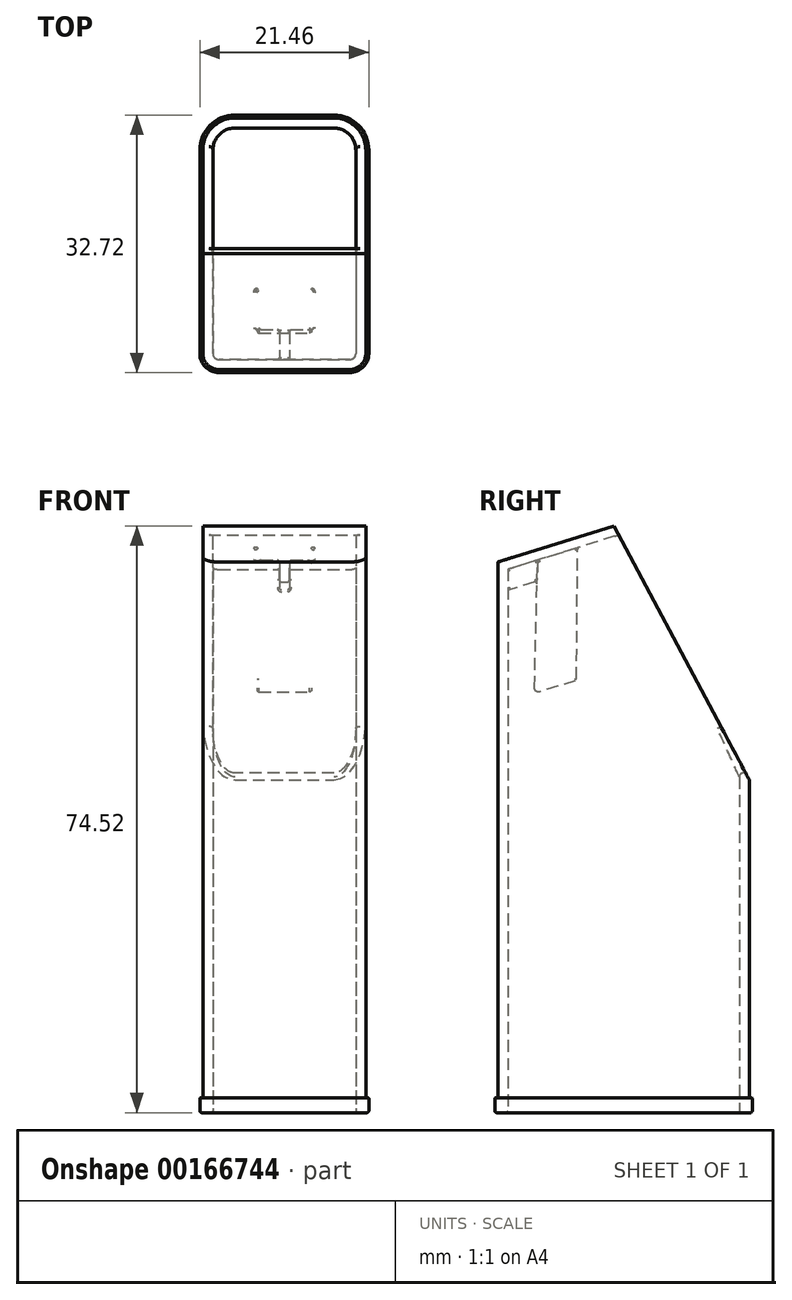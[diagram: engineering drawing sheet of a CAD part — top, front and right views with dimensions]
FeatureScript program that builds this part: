
annotation { "Feature Type Name" : "Feature", "Feature Type Description" : "" }
export const myFeature = defineFeature(function(context is Context, id is Id, definition is map)
    precondition{}
    {
        {
            var Q0;
            Q0=qCreatedBy(makeId("Top.planeOp"),FACE);
            var sketch = newSketch(context, id + "F0", { "sketchPlane" : qUnion([Q0])});
            skLineSegment(sketch, "E0.bottom", {"start": v(10.35, 15.98) * mm, "end": v(-10.35, 15.98) * mm});
            skLineSegment(sketch, "E0.top", {"start": v(10.35, -15.98) * mm, "end": v(-10.35, -15.98) * mm});
            skLineSegment(sketch, "E0.left", {"start": v(10.35, 15.98) * mm, "end": v(10.35, -15.98) * mm});
            skLineSegment(sketch, "E0.right", {"start": v(-10.35, 15.98) * mm, "end": v(-10.35, -15.98) * mm});
            skPoint(sketch, "E0.middle", {"position": v(0, 0) * mm});
            skLineSegment(sketch, "E1.0", {"start": v(10.9, 16.54) * mm, "end": v(-10.9, 16.54) * mm});
            skLineSegment(sketch, "E1.1", {"start": v(10.9, 16.54) * mm, "end": v(10.9, -16.54) * mm});
            skLineSegment(sketch, "E1.2", {"start": v(10.9, -16.54) * mm, "end": v(-10.9, -16.54) * mm});
            skLineSegment(sketch, "E1.3", {"start": v(-10.9, 16.54) * mm, "end": v(-10.9, -16.54) * mm});
            skSolve(sketch);
        }
        {
            var Q0;
            Q0=makeQuery(id+"F0.imprint","IMPRINT",FACE,{"disambiguationData":[TD([[makeQuery(id+"F0.imprint","IMPRINT",EDGE,{"derivedFrom":sQuery(id+"F0.wireOp",EDGE,"E0.bottom")}),1.0]])]});
            extrude(context, id + "F1", {"entities" : qUnion([Q0]), "depth" : 74.52 * mm});
        }
        {
            var Q0;
            Q0=makeQuery(id+"F1.opExtrude","SWEPT_FACE",FACE,{"disambiguationData":[OSD([sQuery(id+"F0.wireOp",EDGE,"E0.left")])]});
            var sketch = newSketch(context, id + "F2", { "sketchPlane" : qUnion([Q0])});
            skLineSegment(sketch, "E2", {"start": v(-1.24, 74.52) * mm, "end": v(-15.98, 69.95) * mm});
            skLineSegment(sketch, "E3", {"start": v(-1.24, 74.52) * mm, "end": v(15.98, 42.3) * mm});
            skSolve(sketch);
        }
        {
            var Q0;
            {var subQ0=sQuery(id+"F2.wireOp",EDGE,"E2");Q0=makeQuery(id+"F2.imprint","IMPRINT",FACE,{"disambiguationData":[TD([[makeQuery(id+"F2.imprint","IMPRINT",EDGE,{"derivedFrom":subQ0}),-1.0]])]});}
            var Q1;
            {var subQ0=sQuery(id+"F2.wireOp",EDGE,"E3");Q1=makeQuery(id+"F2.imprint","IMPRINT",FACE,{"disambiguationData":[TD([[makeQuery(id+"F2.imprint","IMPRINT",EDGE,{"derivedFrom":subQ0}),1.0]])]});}
            extrude(context, id + "F3", {"entities" : qUnion([Q0, Q1]), "operationType" : NewBodyOperationType.REMOVE, "endBound" : BoundingType.UP_TO_NEXT, "oppositeDirection" : true, "depth" : 25.4 * mm});
        }
        {
            var Q0;
            Q0=makeQuery(id+"F1.opExtrude","SWEPT_EDGE",EDGE,{"disambiguationData":[OSD([sQuery(id+"F0.wireOp",EDGE,"E0.top"),sQuery(id+"F0.wireOp",EDGE,"E0.right")])]});
            var Q1;
            Q1=makeQuery(id+"F1.opExtrude","SWEPT_EDGE",EDGE,{"disambiguationData":[OSD([sQuery(id+"F0.wireOp",EDGE,"E0.top"),sQuery(id+"F0.wireOp",EDGE,"E0.left")])]});
            var Q2;
            Q2=makeQuery(id+"F3.boolean.opBoolean","COPY",EDGE,{"derivedFrom":makeQuery(id+"F3.opExtrude","SWEPT_EDGE",EDGE,{"disambiguationData":[OSD([sQuery(id+"F0.wireOp",EDGE,"E0.top"),sQuery(id+"F0.wireOp",EDGE,"E0.left"),sQuery(id+"F2.wireOp",EDGE,"E2")])]})});
            var Q3;
            Q3=makeQuery(id+"F3.boolean.opBoolean","COPY",EDGE,{"derivedFrom":makeQuery(id+"F3.opExtrude","CAP_EDGE",EDGE,{"disambiguationData":[OSD([sQuery(id+"F2.wireOp",EDGE,"E2")])],"isStart":false})});
            var Q4;
            Q4=makeQuery(id+"F3.boolean.opBoolean","COPY",EDGE,{"derivedFrom":makeQuery(id+"F3.opExtrude","CAP_EDGE",EDGE,{"disambiguationData":[OSD([sQuery(id+"F2.wireOp",EDGE,"E2")])],"isStart":true})});
            fillet(context, id + "F4", {"entities" : qUnion([Q0, Q1, Q2, Q3, Q4]), "radius" : 2.03 * mm, "tangentPropagation" : true, "allowEdgeOverflow" : false});
        }
        {
            var Q0;
            Q0=makeQuery(id+"F1.opExtrude","SWEPT_EDGE",EDGE,{"disambiguationData":[OSD([sQuery(id+"F0.wireOp",EDGE,"E0.bottom"),sQuery(id+"F0.wireOp",EDGE,"E0.left")])]});
            var Q1;
            Q1=makeQuery(id+"F1.opExtrude","SWEPT_EDGE",EDGE,{"disambiguationData":[OSD([sQuery(id+"F0.wireOp",EDGE,"E0.bottom"),sQuery(id+"F0.wireOp",EDGE,"E0.right")])]});
            fillet(context, id + "F5", {"entities" : qUnion([Q0, Q1]), "radius" : 4.06 * mm, "tangentPropagation" : true, "allowEdgeOverflow" : false});
        }
        {
            var Q0;
            Q0=makeQuery(id+"F3.boolean.opBoolean","COPY",FACE,{"derivedFrom":makeQuery(id+"F3.opExtrude","SWEPT_FACE",FACE,{"disambiguationData":[OSD([sQuery(id+"F2.wireOp",EDGE,"E3")])]})});
            var Q1;
            Q1=makeQuery(id+"F1.opExtrude","CAP_FACE",FACE,{"disambiguationData":[OSD([sQuery(id+"F0.wireOp",EDGE,"E0.bottom"),sQuery(id+"F0.wireOp",EDGE,"E0.top"),sQuery(id+"F0.wireOp",EDGE,"E0.left"),sQuery(id+"F0.wireOp",EDGE,"E0.right")])],"isStart":true});
            shell(context, id + "F6", {"entities" : qUnion([Q0, Q1]), "thickness" : 1.27 * mm});
        }
        {
            var Q0;
            Q0=makeQuery(id+"F3.boolean.opBoolean","COPY",EDGE,{"derivedFrom":makeQuery(id+"F3.opExtrude","CAP_EDGE",EDGE,{"disambiguationData":[OSD([sQuery(id+"F2.wireOp",EDGE,"E3")])],"isStart":true})});
            var Q1;
            Q1=makeQuery(id+"F6.opShell","OFFSET_EDGE",EDGE,{"disambiguationData":[OSD([sQuery(id+"F2.wireOp",EDGE,"E3")])]});
            fillet(context, id + "F7", {"entities" : qUnion([Q0, Q1]), "radius" : 0.5 * mm, "tangentPropagation" : true, "allowEdgeOverflow" : false});
        }
        {
            var Q0;
            Q0=makeQuery(id+"F1.opExtrude","CAP_FACE",FACE,{"disambiguationData":[OSD([sQuery(id+"F0.wireOp",EDGE,"E0.bottom"),sQuery(id+"F0.wireOp",EDGE,"E0.top"),sQuery(id+"F0.wireOp",EDGE,"E0.left"),sQuery(id+"F0.wireOp",EDGE,"E0.right")])],"isStart":true});
            var sketch = newSketch(context, id + "F8", { "sketchPlane" : qUnion([Q0])});
            skLineSegment(sketch, "E4.0.0", {"start": v(-6.29, -15.98) * mm, "end": v(6.29, -15.98) * mm});
            skArc(sketch, "E4.0.1", {"start": v(6.29, -15.98) * mm, "mid": v(9.16, -14.79) * mm, "end": v(10.35, -11.91) * mm});
            skLineSegment(sketch, "E4.0.2", {"start": v(10.35, -11.91) * mm, "end": v(10.35, 13.94) * mm});
            skArc(sketch, "E4.0.3", {"start": v(10.35, 13.94) * mm, "mid": v(9.76, 15.38) * mm, "end": v(8.32, 15.98) * mm});
            skLineSegment(sketch, "E4.0.4", {"start": v(8.32, 15.98) * mm, "end": v(-8.32, 15.98) * mm});
            skArc(sketch, "E4.0.5", {"start": v(-8.32, 15.98) * mm, "mid": v(-9.76, 15.38) * mm, "end": v(-10.35, 13.94) * mm});
            skLineSegment(sketch, "E4.0.6", {"start": v(-10.35, 13.94) * mm, "end": v(-10.35, -11.91) * mm});
            skArc(sketch, "E4.0.7", {"start": v(-10.35, -11.91) * mm, "mid": v(-9.16, -14.79) * mm, "end": v(-6.29, -15.98) * mm});
            skLineSegment(sketch, "E5.0", {"start": v(8.32, 16.36) * mm, "end": v(-8.32, 16.36) * mm});
            skArc(sketch, "E5.1", {"start": v(10.73, 13.94) * mm, "mid": v(10.02, 15.65) * mm, "end": v(8.32, 16.36) * mm});
            skArc(sketch, "E5.2", {"start": v(-8.32, 16.36) * mm, "mid": v(-10.02, 15.65) * mm, "end": v(-10.73, 13.94) * mm});
            skLineSegment(sketch, "E5.3", {"start": v(10.73, -11.91) * mm, "end": v(10.73, 13.94) * mm});
            skLineSegment(sketch, "E5.4", {"start": v(-10.73, 13.94) * mm, "end": v(-10.73, -11.91) * mm});
            skArc(sketch, "E5.5", {"start": v(-10.73, -11.91) * mm, "mid": v(-9.43, -15.06) * mm, "end": v(-6.29, -16.36) * mm});
            skLineSegment(sketch, "E5.6", {"start": v(-6.29, -16.36) * mm, "end": v(6.29, -16.36) * mm});
            skArc(sketch, "E5.7", {"start": v(6.29, -16.36) * mm, "mid": v(9.43, -15.06) * mm, "end": v(10.73, -11.91) * mm});
            skSolve(sketch);
        }
        {
            var Q0;
            Q0=makeQuery(id+"F8.imprint","IMPRINT",FACE,{"disambiguationData":[TD([[makeQuery(id+"F8.imprint","IMPRINT",EDGE,{"derivedFrom":sQuery(id+"F8.wireOp",EDGE,"E4.0.0")}),1.0]])]});
            extrude(context, id + "F9", {"entities" : qUnion([Q0]), "operationType" : NewBodyOperationType.ADD, "oppositeDirection" : true, "depth" : 1.9 * mm});
        }
        {
            var Q0;
            Q0=makeQuery(id+"F9.boolean.opBoolean","MERGE",FACE,{"derivedFrom":[makeQuery(id+"F1.opExtrude","CAP_FACE",FACE,{"disambiguationData":[OSD([sQuery(id+"F0.wireOp",EDGE,"E0.bottom"),sQuery(id+"F0.wireOp",EDGE,"E0.top"),sQuery(id+"F0.wireOp",EDGE,"E0.left"),sQuery(id+"F0.wireOp",EDGE,"E0.right")])],"isStart":true}),makeQuery(id+"F9.opExtrude","CAP_FACE",FACE,{"disambiguationData":[OSD([sQuery(id+"F8.wireOp",EDGE,"E4.0.0"),sQuery(id+"F8.wireOp",EDGE,"E4.0.1"),sQuery(id+"F8.wireOp",EDGE,"E4.0.2"),sQuery(id+"F8.wireOp",EDGE,"E4.0.3"),sQuery(id+"F8.wireOp",EDGE,"E4.0.4"),sQuery(id+"F8.wireOp",EDGE,"E4.0.5"),sQuery(id+"F8.wireOp",EDGE,"E4.0.6"),sQuery(id+"F8.wireOp",EDGE,"E4.0.7"),sQuery(id+"F8.wireOp",EDGE,"E5.0"),sQuery(id+"F8.wireOp",EDGE,"E5.1"),sQuery(id+"F8.wireOp",EDGE,"E5.2"),sQuery(id+"F8.wireOp",EDGE,"E5.3"),sQuery(id+"F8.wireOp",EDGE,"E5.4"),sQuery(id+"F8.wireOp",EDGE,"E5.5"),sQuery(id+"F8.wireOp",EDGE,"E5.6"),sQuery(id+"F8.wireOp",EDGE,"E5.7")])],"isStart":true})]});
            fillet(context, id + "F10", {"entities" : qUnion([Q0]), "radius" : 0.25 * mm, "tangentPropagation" : true, "allowEdgeOverflow" : false});
        }
        {
            var Q0;
            Q0=makeQuery(id+"F9.opExtrude","CAP_FACE",FACE,{"disambiguationData":[OSD([sQuery(id+"F8.wireOp",EDGE,"E4.0.0"),sQuery(id+"F8.wireOp",EDGE,"E4.0.1"),sQuery(id+"F8.wireOp",EDGE,"E4.0.2"),sQuery(id+"F8.wireOp",EDGE,"E4.0.3"),sQuery(id+"F8.wireOp",EDGE,"E4.0.4"),sQuery(id+"F8.wireOp",EDGE,"E4.0.5"),sQuery(id+"F8.wireOp",EDGE,"E4.0.6"),sQuery(id+"F8.wireOp",EDGE,"E4.0.7"),sQuery(id+"F8.wireOp",EDGE,"E5.0"),sQuery(id+"F8.wireOp",EDGE,"E5.1"),sQuery(id+"F8.wireOp",EDGE,"E5.2"),sQuery(id+"F8.wireOp",EDGE,"E5.3"),sQuery(id+"F8.wireOp",EDGE,"E5.4"),sQuery(id+"F8.wireOp",EDGE,"E5.5"),sQuery(id+"F8.wireOp",EDGE,"E5.6"),sQuery(id+"F8.wireOp",EDGE,"E5.7")])],"isStart":false});
            fillet(context, id + "F11", {"entities" : qUnion([Q0]), "radius" : 0.13 * mm, "tangentPropagation" : true, "allowEdgeOverflow" : false});
        }
        {
            var Q0;
            {var subQ0=sQuery(id+"F2.wireOp",EDGE,"E2");Q0=makeQuery(id+"F6.opShell","OFFSET_FACE",FACE,{"disambiguationData":[OSD([subQ0]),TDD([makeQuery(id+"F3.boolean.opBoolean","COPY",FACE,{"derivedFrom":makeQuery(id+"F3.opExtrude","SWEPT_FACE",FACE,{"disambiguationData":[OSD([subQ0])]})})])]});}
            var sketch = newSketch(context, id + "F12", { "sketchPlane" : qUnion([Q0])});
            skPoint(sketch, "E6.0", {"position": v(0, -21.03) * mm});
            skLineSegment(sketch, "E7.bottom", {"start": v(-3.68, -21.03) * mm, "end": v(3.68, -21.03) * mm});
            skLineSegment(sketch, "E7.top", {"start": v(-3.68, -15.72) * mm, "end": v(3.68, -15.72) * mm});
            skLineSegment(sketch, "E7.left", {"start": v(-3.68, -21.03) * mm, "end": v(-3.68, -15.72) * mm});
            skLineSegment(sketch, "E7.right", {"start": v(3.68, -21.03) * mm, "end": v(3.68, -15.72) * mm});
            skLineSegment(sketch, "E8.0.0", {"start": v(-8.32, -5.03) * mm, "end": v(-8.32, 14.66) * mm});
            skLineSegment(sketch, "E8.0.1", {"start": v(-8.32, 14.66) * mm, "end": v(8.32, 14.66) * mm});
            skLineSegment(sketch, "E8.0.2", {"start": v(8.32, 14.66) * mm, "end": v(8.32, -5.03) * mm});
            skLineSegment(sketch, "E8.0.3", {"start": v(8.32, -5.03) * mm, "end": v(-8.32, -5.03) * mm});
            skSolve(sketch);
        }
        {
            var Q0;
            {var subQ0=sQuery(id+"F12.wireOp",EDGE,"E7.top");Q0=makeQuery(id+"F12.imprint","IMPRINT",FACE,{"disambiguationData":[TD([[makeQuery(id+"F12.imprint","IMPRINT",EDGE,{"derivedFrom":subQ0}),-1.0]])]});}
            cPlane(context, id + "F13", {"entities" : qUnion([Q0]), "cplaneType" : CPlaneType.OFFSET, "offset" : 16.05 * mm, "width" : 152.4 * mm, "height" : 152.4 * mm});
        }
        {
            var Q0;
            Q0=qCreatedBy(id+"F13.planeOp",FACE);
            var sketch = newSketch(context, id + "F14", { "sketchPlane" : qUnion([Q0])});
            skLineSegment(sketch, "E9.0.0", {"start": v(8.32, 13.97) * mm, "end": v(8.32, -6.24) * mm});
            skLineSegment(sketch, "E9.0.1", {"start": v(8.32, 13.97) * mm, "end": v(-8.32, 13.97) * mm});
            skLineSegment(sketch, "E9.0.2", {"start": v(-8.32, 13.97) * mm, "end": v(-8.32, -6.24) * mm});
            skPoint(sketch, "E10", {"position": v(0, -4.96) * mm});
            skLineSegment(sketch, "E11.bottom", {"start": v(-3.45, -10.57) * mm, "end": v(3.45, -10.57) * mm});
            skLineSegment(sketch, "E11.top", {"start": v(-3.45, -4.96) * mm, "end": v(3.45, -4.96) * mm});
            skLineSegment(sketch, "E11.left", {"start": v(-3.45, -10.57) * mm, "end": v(-3.45, -4.96) * mm});
            skLineSegment(sketch, "E11.right", {"start": v(3.45, -10.57) * mm, "end": v(3.45, -4.96) * mm});
            skSolve(sketch);
        }
        {
            var Q0;
            {var subQ5=sQuery(id+"F12.wireOp",EDGE,"E7.top");Q0=makeQuery(id+"F12.imprint","IMPRINT",FACE,{"disambiguationData":[TD([[makeQuery(id+"F12.imprint","IMPRINT",EDGE,{"derivedFrom":subQ5}),1.0]])]});}
            var sketch = newSketch(context, id + "F15", { "sketchPlane" : qUnion([Q0])});
            skLineSegment(sketch, "E12.0", {"start": v(-3.68, -15.72) * mm, "end": v(3.68, -15.72) * mm});
            skLineSegment(sketch, "E13.bottom", {"start": v(-0.64, -15.72) * mm, "end": v(0.63, -15.72) * mm});
            skLineSegment(sketch, "E13.top", {"start": v(-0.64, -5.3) * mm, "end": v(0.63, -5.3) * mm});
            skLineSegment(sketch, "E13.left", {"start": v(-0.64, -15.72) * mm, "end": v(-0.64, -5.3) * mm});
            skLineSegment(sketch, "E13.right", {"start": v(0.63, -15.72) * mm, "end": v(0.63, -5.3) * mm});
            skPoint(sketch, "E14", {"position": v(0, -15.72) * mm});
            skLineSegment(sketch, "E15", {"start": v(-0.64, -13.18) * mm, "end": v(0.63, -13.18) * mm});
            skSolve(sketch);
        }
        {
            var Q0;
            {var subQ0=sQuery(id+"F2.wireOp",EDGE,"E2");Q0=makeQuery(id+"F6.opShell","OFFSET_FACE",FACE,{"disambiguationData":[OSD([subQ0]),TDD([makeQuery(id+"F3.boolean.opBoolean","COPY",FACE,{"derivedFrom":makeQuery(id+"F3.opExtrude","SWEPT_FACE",FACE,{"disambiguationData":[OSD([subQ0])]})})])]});}
            var sketch = newSketch(context, id + "F16", { "sketchPlane" : qUnion([Q0])});
            skPoint(sketch, "E16.0", {"position": v(-3.68, -21.03) * mm});
            skLineSegment(sketch, "E17.bottom", {"start": v(-3.68, -15.7) * mm, "end": v(3.68, -15.7) * mm});
            skLineSegment(sketch, "E17.top", {"start": v(-3.68, -10.39) * mm, "end": v(3.68, -10.39) * mm});
            skLineSegment(sketch, "E17.left", {"start": v(-3.68, -15.7) * mm, "end": v(-3.68, -10.39) * mm});
            skLineSegment(sketch, "E17.right", {"start": v(3.68, -15.7) * mm, "end": v(3.68, -10.39) * mm});
            skSolve(sketch);
        }
        {
            var Q1;
            Q1=makeQuery(id+"F16.imprint","IMPRINT",FACE,{"disambiguationData":[TD([[makeQuery(id+"F16.imprint","IMPRINT",EDGE,{"derivedFrom":sQuery(id+"F16.wireOp",EDGE,"E17.bottom")}),1.0]])]});
            var Q2;
            Q2=makeQuery(id+"F14.imprint","IMPRINT",FACE,{"disambiguationData":[TD([[makeQuery(id+"F14.imprint","IMPRINT",EDGE,{"derivedFrom":sQuery(id+"F14.wireOp",EDGE,"E11.bottom")}),1.0]])]});
            loft(context, id + "F17", {"operationType" : NewBodyOperationType.ADD, "sheetProfilesArray" : [{ "sheetProfileEntities" : qUnion([Q1]) }, { "sheetProfileEntities" : qUnion([Q2]) }]});
        }
        {
            var Q0;
            {var subQ0=sQuery(id+"F15.wireOp",EDGE,"E13.top");Q0=makeQuery(id+"F15.imprint","IMPRINT",FACE,{"disambiguationData":[TD([[makeQuery(id+"F15.imprint","IMPRINT",EDGE,{"derivedFrom":subQ0}),-1.0]])]});}
            var Q1;
            {var subQ0=sQuery(id+"F15.wireOp",EDGE,"E15");Q1=makeQuery(id+"F15.imprint","IMPRINT",FACE,{"disambiguationData":[TD([[makeQuery(id+"F15.imprint","IMPRINT",EDGE,{"derivedFrom":subQ0}),1.0]])]});}
            extrude(context, id + "F18", {"entities" : qUnion([Q0, Q1]), "operationType" : NewBodyOperationType.ADD, "depth" : 2.54 * mm});
        }
        {
            var Q0;
            Q0=makeQuery(id+"F17.opLoft","MID_CAP_EDGE",EDGE,{"disambiguationData":[OSD([sQuery(id+"F14.wireOp",EDGE,"E11.top"),sQuery(id+"F14.wireOp",EDGE,"E11.left"),sQuery(id+"F14.wireOp",EDGE,"E11.right")])],"capPos":1.0});
            fillet(context, id + "F19", {"entities" : qUnion([Q0]), "radius" : 0.5 * mm, "tangentPropagation" : true, "allowEdgeOverflow" : false});
        }
        {
            var Q0;
            Q0=makeQuery(id+"F17.opLoft","SWEPT_FACE",FACE,{"disambiguationData":[OSD([sQuery(id+"F14.wireOp",EDGE,"E11.bottom"),sQuery(id+"F14.wireOp",EDGE,"E11.left"),sQuery(id+"F14.wireOp",EDGE,"E11.right"),sQuery(id+"F16.wireOp",EDGE,"E17.bottom"),sQuery(id+"F16.wireOp",EDGE,"E17.left"),sQuery(id+"F16.wireOp",EDGE,"E17.right")])]});
            var Q1;
            Q1=makeQuery(id+"F17.opLoft","SWEPT_FACE",FACE,{"disambiguationData":[OSD([sQuery(id+"F14.wireOp",EDGE,"E11.bottom"),sQuery(id+"F14.wireOp",EDGE,"E11.top"),sQuery(id+"F14.wireOp",EDGE,"E11.right"),sQuery(id+"F16.wireOp",EDGE,"E17.bottom"),sQuery(id+"F16.wireOp",EDGE,"E17.top"),sQuery(id+"F16.wireOp",EDGE,"E17.right")])]});
            var Q2;
            Q2=makeQuery(id+"F17.opLoft","SWEPT_FACE",FACE,{"disambiguationData":[OSD([sQuery(id+"F14.wireOp",EDGE,"E11.bottom"),sQuery(id+"F14.wireOp",EDGE,"E11.top"),sQuery(id+"F14.wireOp",EDGE,"E11.left"),sQuery(id+"F16.wireOp",EDGE,"E17.bottom"),sQuery(id+"F16.wireOp",EDGE,"E17.top"),sQuery(id+"F16.wireOp",EDGE,"E17.left")])]});
            fillet(context, id + "F20", {"entities" : qUnion([Q0, Q1, Q2]), "radius" : 0.25 * mm, "tangentPropagation" : true, "allowEdgeOverflow" : false});
        }
        {
            var Q0;
            Q0=makeQuery(id+"F18.opExtrude","SWEPT_FACE",FACE,{"disambiguationData":[OSD([sQuery(id+"F15.wireOp",EDGE,"E13.right")])]});
            var Q1;
            Q1=makeQuery(id+"F18.opExtrude","SWEPT_FACE",FACE,{"disambiguationData":[OSD([sQuery(id+"F15.wireOp",EDGE,"E13.left")])]});
            var Q2;
            Q2=makeQuery(id+"F18.boolean.opBoolean","INTERSECT",EDGE,{"derivedFrom":[makeQuery(id+"F17.opLoft","SWEPT_FACE",FACE,{"disambiguationData":[OSD([sQuery(id+"F14.wireOp",EDGE,"E11.top"),sQuery(id+"F14.wireOp",EDGE,"E11.left"),sQuery(id+"F14.wireOp",EDGE,"E11.right"),sQuery(id+"F16.wireOp",EDGE,"E17.top"),sQuery(id+"F16.wireOp",EDGE,"E17.left"),sQuery(id+"F16.wireOp",EDGE,"E17.right")])]}),makeQuery(id+"F18.opExtrude","CAP_FACE",FACE,{"disambiguationData":[OSD([sQuery(id+"F15.wireOp",EDGE,"E13.bottom"),sQuery(id+"F15.wireOp",EDGE,"E13.top"),sQuery(id+"F15.wireOp",EDGE,"E13.left"),sQuery(id+"F15.wireOp",EDGE,"E13.right")])],"isStart":false})]});
            var Q3;
            Q3=makeQuery(id+"F18.boolean.opBoolean","INTERSECT",EDGE,{"derivedFrom":[makeQuery(id+"F6.opShell","OFFSET_FACE",FACE,{"disambiguationData":[OSD([sQuery(id+"F0.wireOp",EDGE,"E0.top")])]}),makeQuery(id+"F18.opExtrude","CAP_FACE",FACE,{"disambiguationData":[OSD([sQuery(id+"F15.wireOp",EDGE,"E13.bottom"),sQuery(id+"F15.wireOp",EDGE,"E13.top"),sQuery(id+"F15.wireOp",EDGE,"E13.left"),sQuery(id+"F15.wireOp",EDGE,"E13.right")])],"isStart":false})]});
            fillet(context, id + "F21", {"entities" : qUnion([Q0, Q1, Q2, Q3]), "radius" : 0.25 * mm, "tangentPropagation" : true, "allowEdgeOverflow" : false});
        }
    });
